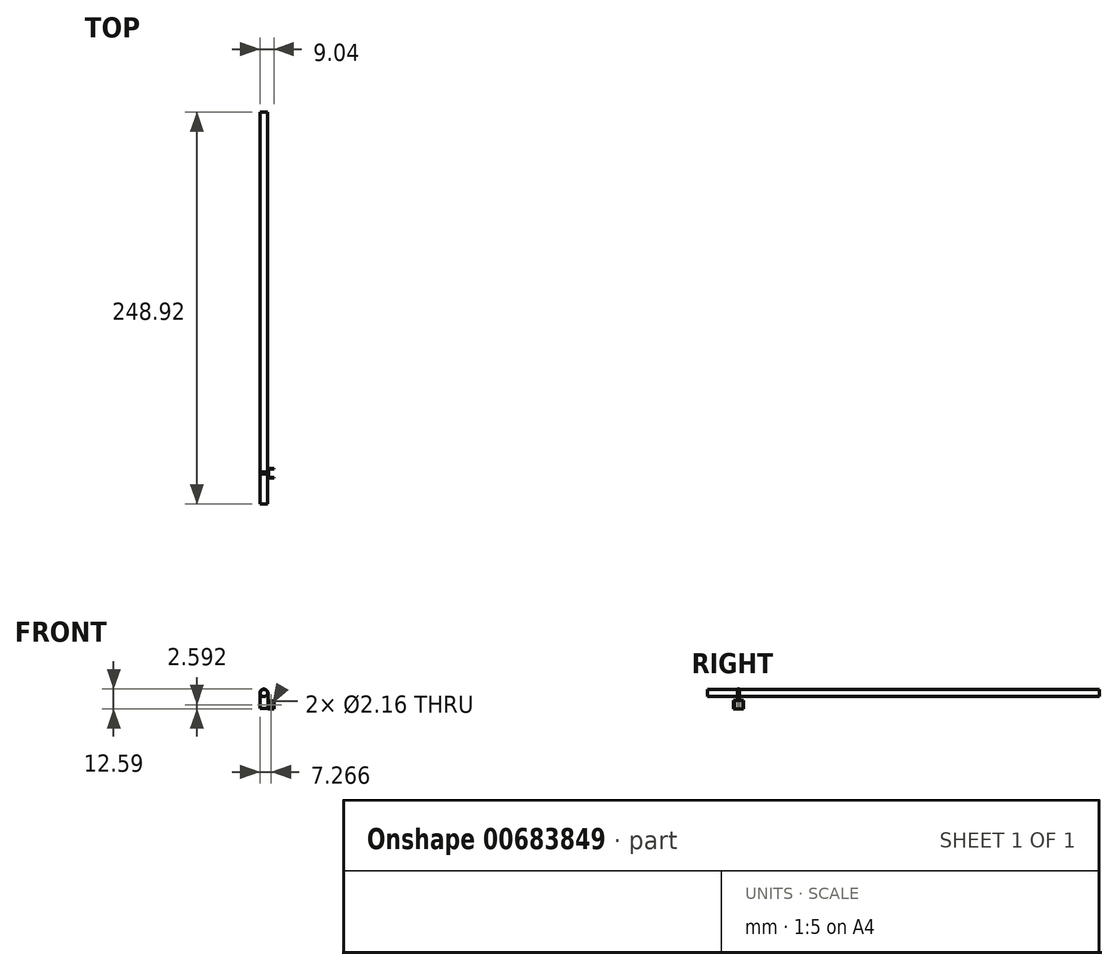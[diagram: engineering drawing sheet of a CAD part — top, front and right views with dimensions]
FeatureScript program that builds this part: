
annotation { "Feature Type Name" : "Feature", "Feature Type Description" : "" }
export const myFeature = defineFeature(function(context is Context, id is Id, definition is map)
    precondition{}
    {
        {
            var Q0;
            Q0=qCreatedBy(makeId("Front.planeOp"),FACE);
            var sketch = newSketch(context, id + "F0", { "sketchPlane" : qUnion([Q0])});
            skCircle(sketch, "E0", {"center": v(0, 5.4) * mm, "radius": 2.56 * mm});
            skArc(sketch, "E1", {"start": v(0, 2.56) * mm, "mid": v(-0.36, 2.53) * mm, "end": v(-0.72, 2.45) * mm});
            skLineSegment(sketch, "E2", {"start": v(2.56, 5.4) * mm, "end": v(2.56, 1.72) * mm});
            skLineSegment(sketch, "E3", {"start": v(-2.56, 5.4) * mm, "end": v(-2.56, 4.38) * mm});
            skArc(sketch, "E4.MirrorC", {"start": v(-11.6, 2.55) * mm, "mid": v(-11.6, 2.55) * mm, "end": v(-11.6, 2.55) * mm});
            skPoint(sketch, "E5.start.orphan", {"position": v(0, -2.56) * mm});
            skPoint(sketch, "E6.start.orphan", {"position": v(0, 2.56) * mm});
            skPoint(sketch, "E7.orphan", {"position": v(2.56, 0) * mm});
            skPoint(sketch, "E8.orphan", {"position": v(-2.56, 0) * mm});
            skLineSegment(sketch, "E9", {"start": v(-2.56, 4.38) * mm, "end": v(-2.56, -2.83) * mm});
            skLineSegment(sketch, "E10", {"start": v(2.56, 1.72) * mm, "end": v(2.52, -2.83) * mm});
            skPoint(sketch, "E10.endSnap0", {"position": v(2.44, 0.77) * mm});
            skPoint(sketch, "E11.start.orphan", {"position": v(2.56, 4.18) * mm});
            skLineSegment(sketch, "E12", {"start": v(-2.56, 5.4) * mm, "end": v(-2.56, -2.83) * mm});
            skPoint(sketch, "E13.end.orphan", {"position": v(2.44, -13.4) * mm});
            skLineSegment(sketch, "E14", {"start": v(-2.56, -2.83) * mm, "end": v(-2.56, -4.37) * mm});
            skLineSegment(sketch, "E15", {"start": v(2.52, -2.83) * mm, "end": v(2.52, -4.37) * mm});
            skLineSegment(sketch, "E16", {"start": v(-2.56, -4.37) * mm, "end": v(2.52, -4.37) * mm});
            skSolve(sketch);
        }
        {
            var Q0;
            {var subQ0=sQuery(id+"F0.wireOp",EDGE,"E0");var subQ1=makeQuery(id+"F0.imprint","INTERSECT",VERTEX,{"derivedFrom":[subQ0,sQuery(id+"F0.wireOp",EDGE,"E2")]});Q0=makeQuery(id+"F0.imprint","IMPRINT",FACE,{"disambiguationData":[TD([[makeQuery(id+"F0.imprint","IMPRINT",EDGE,{"disambiguationData":[TD([[subQ1,1.0]])],"derivedFrom":subQ0}),1.0]])]});}
            var Q1;
            {var subQ0=sQuery(id+"F0.wireOp",EDGE,"E3");Q1=makeQuery(id+"F0.imprint","IMPRINT",FACE,{"disambiguationData":[TD([[makeQuery(id+"F0.imprint","IMPRINT",EDGE,{"derivedFrom":subQ0}),1.0]])]});}
            var Q2;
            {var subQ0=sQuery(id+"F0.wireOp",EDGE,"E2");var subQ1=sQuery(id+"F0.wireOp",EDGE,"E1");var subQ2=makeQuery(id+"F0.imprint","INTERSECT",VERTEX,{"derivedFrom":[subQ1,subQ0]});Q2=makeQuery(id+"F0.imprint","IMPRINT",FACE,{"disambiguationData":[TD([[makeQuery(id+"F0.imprint","IMPRINT",EDGE,{"disambiguationData":[TD([[subQ2,-1.0]])],"derivedFrom":subQ1}),-1.0]])]});}
            var Q3;
            {var subQ0=sQuery(id+"F0.wireOp",EDGE,"E1");var subQ1=makeQuery(id+"F0.imprint","INTERSECT",VERTEX,{"derivedFrom":[subQ0,sQuery(id+"F0.wireOp",EDGE,"E3")]});Q3=makeQuery(id+"F0.imprint","IMPRINT",FACE,{"disambiguationData":[TD([[makeQuery(id+"F0.imprint","IMPRINT",EDGE,{"disambiguationData":[TD([[subQ1,1.0]])],"derivedFrom":subQ0}),1.0]])]});}
            var Q4;
            {var subQ0=sQuery(id+"F0.wireOp",EDGE,"263fcdb8-d820-4d45-9f7c-0084accf3f070.MirrorCS");Q4=makeQuery(id+"F0.imprint","IMPRINT",FACE,{"disambiguationData":[TD([[makeQuery(id+"F0.imprint","IMPRINT",EDGE,{"derivedFrom":subQ0}),1.0]])]});}
            var Q5;
            {var subQ0=sQuery(id+"F0.wireOp",EDGE,"nn3kji8N-mWU8-6sac-MlCo-DN8aCnxxy875");Q5=makeQuery(id+"F0.imprint","IMPRINT",FACE,{"disambiguationData":[TD([[makeQuery(id+"F0.imprint","IMPRINT",EDGE,{"derivedFrom":subQ0}),-1.0]])]});}
            var Q6;
            {var subQ1=sQuery(id+"F0.wireOp",EDGE,"nn3kji8N-mWU8-6sac-MlCo-DN8aCnxxy875");Q6=makeQuery(id+"F0.imprint","IMPRINT",FACE,{"disambiguationData":[TD([[makeQuery(id+"F0.imprint","IMPRINT",EDGE,{"derivedFrom":subQ1}),1.0]])]});}
            var Q7;
            {var subQ0=sQuery(id+"F0.wireOp",EDGE,"G4lSKCHw-J7V3-nXiF-vaOj-cBAkdTGiRsgI");var subQ1=sQuery(id+"F0.wireOp",EDGE,"E2");var subQ2=makeQuery(id+"F0.imprint","INTERSECT",VERTEX,{"derivedFrom":[subQ1,subQ0]});Q7=makeQuery(id+"F0.imprint","IMPRINT",FACE,{"disambiguationData":[TD([[makeQuery(id+"F0.imprint","IMPRINT",EDGE,{"disambiguationData":[TD([[subQ2,-1.0]])],"derivedFrom":subQ1}),-1.0]])]});}
            var Q8;
            {var subQ1=sQuery(id+"F0.wireOp",EDGE,"cd80d73e-9bc2-4dc0-84be-316595012ded0.MirrorCS");Q8=makeQuery(id+"F0.imprint","IMPRINT",FACE,{"disambiguationData":[TD([[makeQuery(id+"F0.imprint","IMPRINT",EDGE,{"derivedFrom":subQ1}),-1.0]])]});}
            var Q9;
            {var subQ0=sQuery(id+"F0.wireOp",EDGE,"E2");var subQ1=sQuery(id+"F0.wireOp",EDGE,"E1");var subQ2=makeQuery(id+"F0.imprint","INTERSECT",VERTEX,{"derivedFrom":[subQ1,subQ0]});Q9=makeQuery(id+"F0.imprint","IMPRINT",FACE,{"disambiguationData":[TD([[makeQuery(id+"F0.imprint","IMPRINT",EDGE,{"disambiguationData":[TD([[subQ2,1.0]])],"derivedFrom":subQ1}),-1.0]])]});}
            var Q10;
            {var subQ0=sQuery(id+"F0.wireOp",EDGE,"kcDJH2sf-21BA-L9Yy-qe85-3mtlSAZsPEdo");Q10=makeQuery(id+"F0.imprint","IMPRINT",FACE,{"disambiguationData":[TD([[makeQuery(id+"F0.imprint","IMPRINT",EDGE,{"derivedFrom":subQ0}),1.0]])]});}
            var Q11;
            {var subQ0=sQuery(id+"F0.wireOp",EDGE,"WZRXunty-gl11-gvDB-eq7a-ggUTLZATC6E6");Q11=makeQuery(id+"F0.imprint","IMPRINT",FACE,{"disambiguationData":[TD([[makeQuery(id+"F0.imprint","IMPRINT",EDGE,{"derivedFrom":subQ0}),1.0]])]});}
            var Q12;
            {var subQ6=sQuery(id+"F0.wireOp",EDGE,"E9");Q12=makeQuery(id+"F0.imprint","IMPRINT",FACE,{"disambiguationData":[TD([[makeQuery(id+"F0.imprint","IMPRINT",EDGE,{"derivedFrom":subQ6}),1.0]])]});}
            var Q13;
            {var subQ3=sQuery(id+"F0.wireOp",EDGE,"mmOzPl4o-ixsb-ohx5-I9sC-uw6xFzwwk5XC");Q13=makeQuery(id+"F0.imprint","IMPRINT",FACE,{"disambiguationData":[TD([[makeQuery(id+"F0.imprint","IMPRINT",EDGE,{"derivedFrom":subQ3}),1.0]])]});}
            extrude(context, id + "F1", {"entities" : qUnion([Q0, Q1, Q2, Q3, Q4, Q5, Q6, Q7, Q8, Q9, Q10, Q11, Q12, Q13]), "oppositeDirection" : true, "depth" : 1.27 * mm, "offsetDistance" : 25.4 * mm});
        }
        {
            var Q0;
            Q0=makeQuery(id+"F1.opExtrude","CAP_FACE",FACE,{"disambiguationData":[OSD([sQuery(id+"F0.wireOp",EDGE,"NQC7D4eD-zXav-Hkey-WBNL-hidIfPrPsmmw"),sQuery(id+"F0.wireOp",EDGE,"Y8T2P4YK-4LtQ-yw2D-mTcZ-RdnlM3RRqPwx"),sQuery(id+"F0.wireOp",EDGE,"ErvJBt9r-b4Zx-H6VP-9QHq-hFwdqEP6Mpm7"),sQuery(id+"F0.wireOp",EDGE,"E0")])],"isStart":false});
            var sketch = newSketch(context, id + "F2", { "sketchPlane" : qUnion([Q0])});
            skCircle(sketch, "E17", {"center": v(0, 5.4) * mm, "radius": 2.29 * mm});
            skSolve(sketch);
        }
        {
            var Q0;
            Q0=makeQuery(id+"F2.imprint","IMPRINT",FACE,{"disambiguationData":[TD([[makeQuery(id+"F2.imprint","IMPRINT",EDGE,{"derivedFrom":sQuery(id+"F2.wireOp",EDGE,"E17")}),1.0]])]});
            extrude(context, id + "F3", {"entities" : qUnion([Q0]), "operationType" : NewBodyOperationType.ADD, "depth" : 228.6 * mm, "offsetDistance" : 25.4 * mm, "hasSecondDirection" : true, "secondDirectionOppositeDirection" : true, "secondDirectionDepth" : 20.32 * mm});
        }
        {
            var Q0;
            Q0=makeQuery(id+"F1.opExtrude","SWEPT_FACE",FACE,{"disambiguationData":[OSD([sQuery(id+"F0.wireOp",EDGE,"E10")])]});
            var sketch = newSketch(context, id + "F4", { "sketchPlane" : qUnion([Q0])});
            skLineSegment(sketch, "E18.bottom", {"start": v(3.66, -4.58) * mm, "end": v(-2.5, -4.58) * mm});
            skLineSegment(sketch, "E18.top", {"start": v(3.66, 0.6) * mm, "end": v(-2.5, 0.6) * mm});
            skLineSegment(sketch, "E18.left", {"start": v(3.66, -4.58) * mm, "end": v(3.66, 0.6) * mm});
            skLineSegment(sketch, "E18.right", {"start": v(-2.5, -4.58) * mm, "end": v(-2.5, 0.6) * mm});
            skPoint(sketch, "E18.middle.positionSnap0", {"position": v(0, 0) * mm});
            skPoint(sketch, "E18.centerSnap0", {"position": v(0, 0) * mm});
            skSolve(sketch);
        }
        {
            var Q0;
            {var subQ0=sQuery(id+"F4.wireOp",EDGE,"E18.left");Q0=makeQuery(id+"F4.imprint","IMPRINT",FACE,{"disambiguationData":[TD([[makeQuery(id+"F4.imprint","IMPRINT",EDGE,{"derivedFrom":subQ0}),1.0]])]});}
            var Q1;
            {var subQ0=sQuery(id+"F4.wireOp",EDGE,"E18.right");Q1=makeQuery(id+"F4.imprint","IMPRINT",FACE,{"disambiguationData":[TD([[makeQuery(id+"F4.imprint","IMPRINT",EDGE,{"derivedFrom":subQ0}),-1.0]])]});}
            var Q2;
            {var subQ1=sQuery(id+"F0.wireOp",EDGE,"0STaALuz-qcVV-emnR-7TsT-yvQYUWInrF14");var subQ6=makeQuery(id+"F1.opExtrude","SWEPT_EDGE",EDGE,{"disambiguationData":[OSD([sQuery(id+"F0.wireOp",EDGE,"WZRXunty-gl11-gvDB-eq7a-ggUTLZATC6E6"),subQ1,sQuery(id+"F0.wireOp",EDGE,"E11")])]});Q2=makeQuery(id+"F4.imprint","IMPRINT",FACE,{"disambiguationData":[TD([[makeQuery(id+"F4.imprint","IMPRINT",EDGE,{"derivedFrom":subQ6}),1.0]])]});}
            var Q3;
            {var subQ0=sQuery(id+"F4.wireOp",EDGE,"E18.bottom");var subQ1=sQuery(id+"F0.wireOp",EDGE,"0STaALuz-qcVV-emnR-7TsT-yvQYUWInrF14");var subQ2=makeQuery(id+"F1.opExtrude","CAP_EDGE",EDGE,{"disambiguationData":[OSD([subQ1])],"isStart":false});var subQ3=makeQuery(id+"F4.imprint","INTERSECT",VERTEX,{"derivedFrom":[subQ2,subQ0]});Q3=makeQuery(id+"F4.imprint","IMPRINT",FACE,{"disambiguationData":[TD([[makeQuery(id+"F4.imprint","IMPRINT",EDGE,{"disambiguationData":[TD([[subQ3,-1.0]])],"derivedFrom":subQ0}),-1.0]])]});}
            var Q4;
            {var subQ1=sQuery(id+"F0.wireOp",EDGE,"0STaALuz-qcVV-emnR-7TsT-yvQYUWInrF14");var subQ6=makeQuery(id+"F1.opExtrude","SWEPT_EDGE",EDGE,{"disambiguationData":[OSD([subQ1,sQuery(id+"F0.wireOp",EDGE,"YwyUZhCz-AFjn-tTO7-jNPe-idEtptmNyLsH")])]});Q4=makeQuery(id+"F4.imprint","IMPRINT",FACE,{"disambiguationData":[TD([[makeQuery(id+"F4.imprint","IMPRINT",EDGE,{"derivedFrom":subQ6}),-1.0]])]});}
            var Q5;
            {var subQ1=sQuery(id+"F0.wireOp",EDGE,"E10");var subQ6=makeQuery(id+"F1.opExtrude","SWEPT_EDGE",EDGE,{"disambiguationData":[OSD([subQ1,sQuery(id+"F0.wireOp",EDGE,"mmOzPl4o-ixsb-ohx5-I9sC-uw6xFzwwk5XC")])]});Q5=makeQuery(id+"F4.imprint","IMPRINT",FACE,{"disambiguationData":[TD([[makeQuery(id+"F4.imprint","IMPRINT",EDGE,{"derivedFrom":subQ6}),-1.0]])]});}
            extrude(context, id + "F5", {"entities" : qUnion([Q0, Q1, Q2, Q3, Q4, Q5]), "depth" : 3.94 * mm, "offsetDistance" : 25.4 * mm});
        }
        {
            var Q0;
            Q0=makeQuery(id+"F5.opExtrude","CAP_FACE",FACE,{"disambiguationData":[OSD([sQuery(id+"F0.wireOp",EDGE,"WZRXunty-gl11-gvDB-eq7a-ggUTLZATC6E6"),sQuery(id+"F0.wireOp",EDGE,"0STaALuz-qcVV-emnR-7TsT-yvQYUWInrF14"),sQuery(id+"F0.wireOp",EDGE,"E11"),sQuery(id+"F4.wireOp",EDGE,"E18.bottom"),sQuery(id+"F4.wireOp",EDGE,"E18.top"),sQuery(id+"F4.wireOp",EDGE,"E18.left"),sQuery(id+"F4.wireOp",EDGE,"E18.right")])],"isStart":false});
            var Q1;
            {var subQ0=sQuery(id+"F4.wireOp",EDGE,"E18.top");Q1=makeQuery(id+"F5.opExtrude","SWEPT_FACE",FACE,{"disambiguationData":[OSD([subQ0]),TDD([makeQuery(id+"F4.imprint","IMPRINT",EDGE,{"disambiguationData":[TD([[makeQuery(id+"F4.imprint","INTERSECT",VERTEX,{"derivedFrom":[subQ0,sQuery(id+"F4.wireOp",EDGE,"E18.left")]}),-1.0]])],"derivedFrom":subQ0})])]});}
            var Q2;
            {var subQ0=sQuery(id+"F4.wireOp",EDGE,"E18.top");Q2=makeQuery(id+"F5.opExtrude","SWEPT_FACE",FACE,{"disambiguationData":[OSD([subQ0]),TDD([makeQuery(id+"F4.imprint","IMPRINT",EDGE,{"disambiguationData":[TD([[makeQuery(id+"F4.imprint","INTERSECT",VERTEX,{"derivedFrom":[subQ0,sQuery(id+"F4.wireOp",EDGE,"E18.right")]}),1.0]])],"derivedFrom":subQ0})])]});}
            var Q3;
            Q3=makeQuery(id+"F5.opExtrude","SWEPT_FACE",FACE,{"disambiguationData":[OSD([sQuery(id+"F4.wireOp",EDGE,"E18.bottom")])]});
            var Q4;
            Q4=makeQuery(id+"F5.opExtrude","SWEPT_FACE",FACE,{"disambiguationData":[OSD([sQuery(id+"F0.wireOp",EDGE,"WZRXunty-gl11-gvDB-eq7a-ggUTLZATC6E6"),sQuery(id+"F0.wireOp",EDGE,"0STaALuz-qcVV-emnR-7TsT-yvQYUWInrF14"),sQuery(id+"F0.wireOp",EDGE,"E11")])]});
            shell(context, id + "F6", {"entities" : qUnion([Q0, Q1, Q2, Q3, Q4]), "thickness" : 0.38 * mm});
        }
        {
            var Q0;
            Q0=makeQuery(id+"F5.opExtrude","SWEPT_FACE",FACE,{"disambiguationData":[OSD([sQuery(id+"F4.wireOp",EDGE,"E18.right")])]});
            var sketch = newSketch(context, id + "F7", { "sketchPlane" : qUnion([Q0])});
            skCircle(sketch, "E19", {"center": v(4.7, -2.04) * mm, "radius": 1.08 * mm});
            skSolve(sketch);
        }
        {
            var Q0;
            Q0=qSketchRegion(id+"F7",true);
            extrude(context, id + "F8", {"entities" : qUnion([Q0]), "operationType" : NewBodyOperationType.REMOVE, "oppositeDirection" : true, "depth" : 11.18 * mm, "offsetDistance" : 25.4 * mm});
        }
    });
